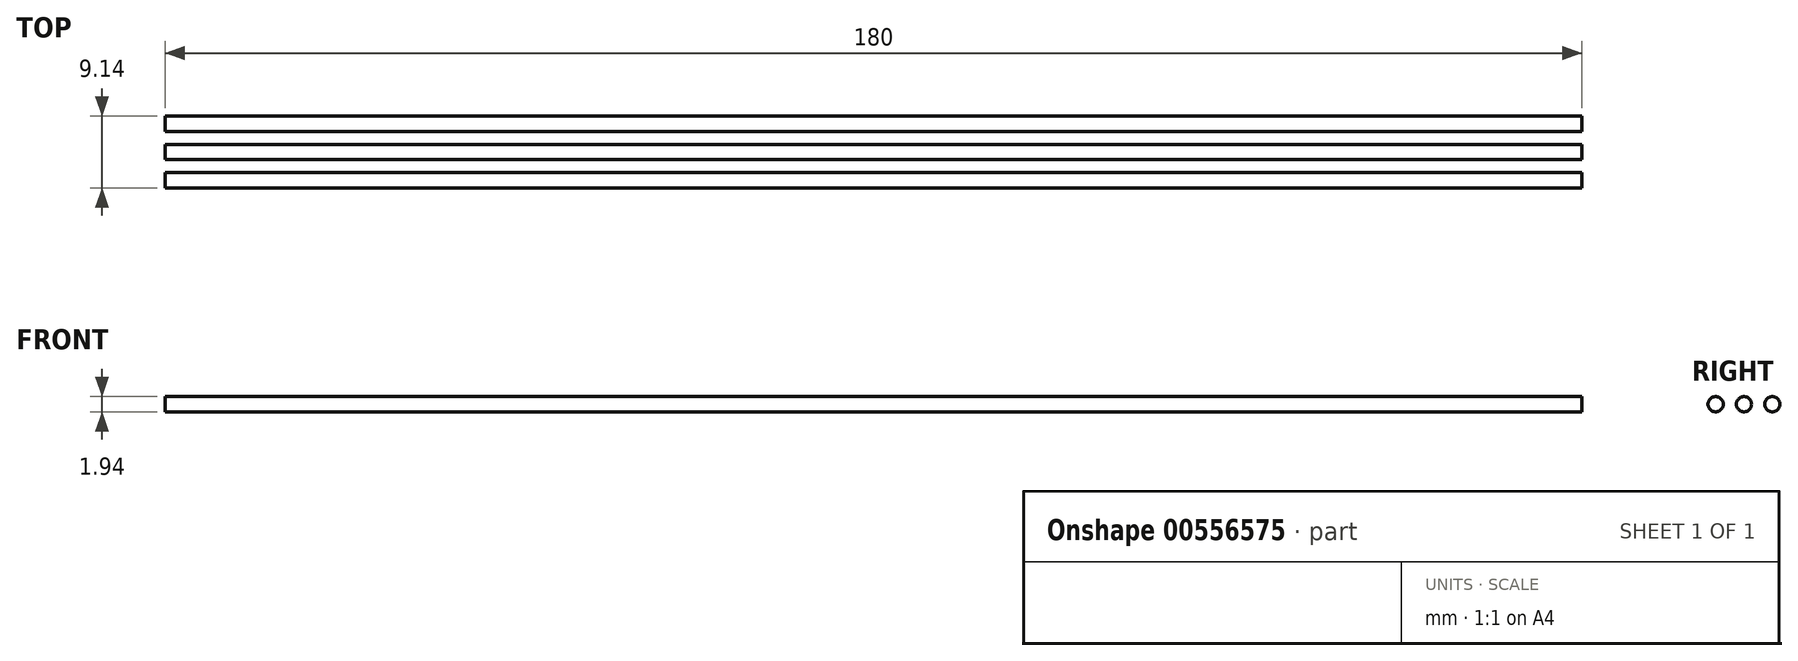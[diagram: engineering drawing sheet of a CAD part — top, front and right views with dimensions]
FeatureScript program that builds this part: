
annotation { "Feature Type Name" : "Feature", "Feature Type Description" : "" }
export const myFeature = defineFeature(function(context is Context, id is Id, definition is map)
    precondition{}
    {
        {
            var Q0;
            Q0=qCreatedBy(makeId("Right.planeOp"),FACE);
            var sketch = newSketch(context, id + "F0", { "sketchPlane" : qUnion([Q0])});
            skCircle(sketch, "E0", {"center": v(0, 0) * mm, "radius": 0.97 * mm});
            skCircle(sketch, "E1.1.0.0", {"center": v(0, -3.6) * mm, "radius": 0.97 * mm});
            skCircle(sketch, "E1.2.0.0", {"center": v(0, -7.2) * mm, "radius": 0.97 * mm});
            skLineSegment(sketch, "E1.direction1", {"start": v(0, 0) * mm, "end": v(0, -3.6) * mm, "construction": true});
            skSolve(sketch);
        }
        {
            var Q0;
            Q0=sQuery(id+"F0.wireOp",EDGE,"E0");
            var Q1;
            Q1=sQuery(id+"F0.wireOp",EDGE,"E1.1.0.0");
            var Q2;
            Q2=sQuery(id+"F0.wireOp",EDGE,"E1.2.0.0");
            extrude(context, id + "F1", {"bodyType" : ExtendedToolBodyType.SURFACE, "surfaceEntities" : qUnion([Q0, Q1, Q2]), "depth" : 180 * mm, "offsetDistance" : 25 * mm});
        }
        {
            var Q0;
            Q0=makeQuery(id+"F1.opExtrude","SWEPT_BODY",BODY,{"disambiguationData":[OSD([sQuery(id+"F0.wireOp",EDGE,"E0")])]});
            var Q1;
            Q1=makeQuery(id+"F1.opExtrude","SWEPT_BODY",BODY,{"disambiguationData":[OSD([sQuery(id+"F0.wireOp",EDGE,"E1.1.0.0")])]});
            var Q2;
            Q2=makeQuery(id+"F1.opExtrude","SWEPT_BODY",BODY,{"disambiguationData":[OSD([sQuery(id+"F0.wireOp",EDGE,"E1.2.0.0")])]});
            var Q3;
            Q3=makeQuery(id+"F1.opExtrude","SWEPT_FACE",FACE,{"disambiguationData":[OSD([sQuery(id+"F0.wireOp",EDGE,"E0")])]});
            transform(context, id + "F2", {"entities" : qUnion([Q0, Q1, Q2]), "transformType" : TransformType.ROTATION, "transformAxis" : qUnion([Q3]), "angle" : 90 * degree, "oppositeDirection" : true, "makeCopy" : false});
        }
    });
